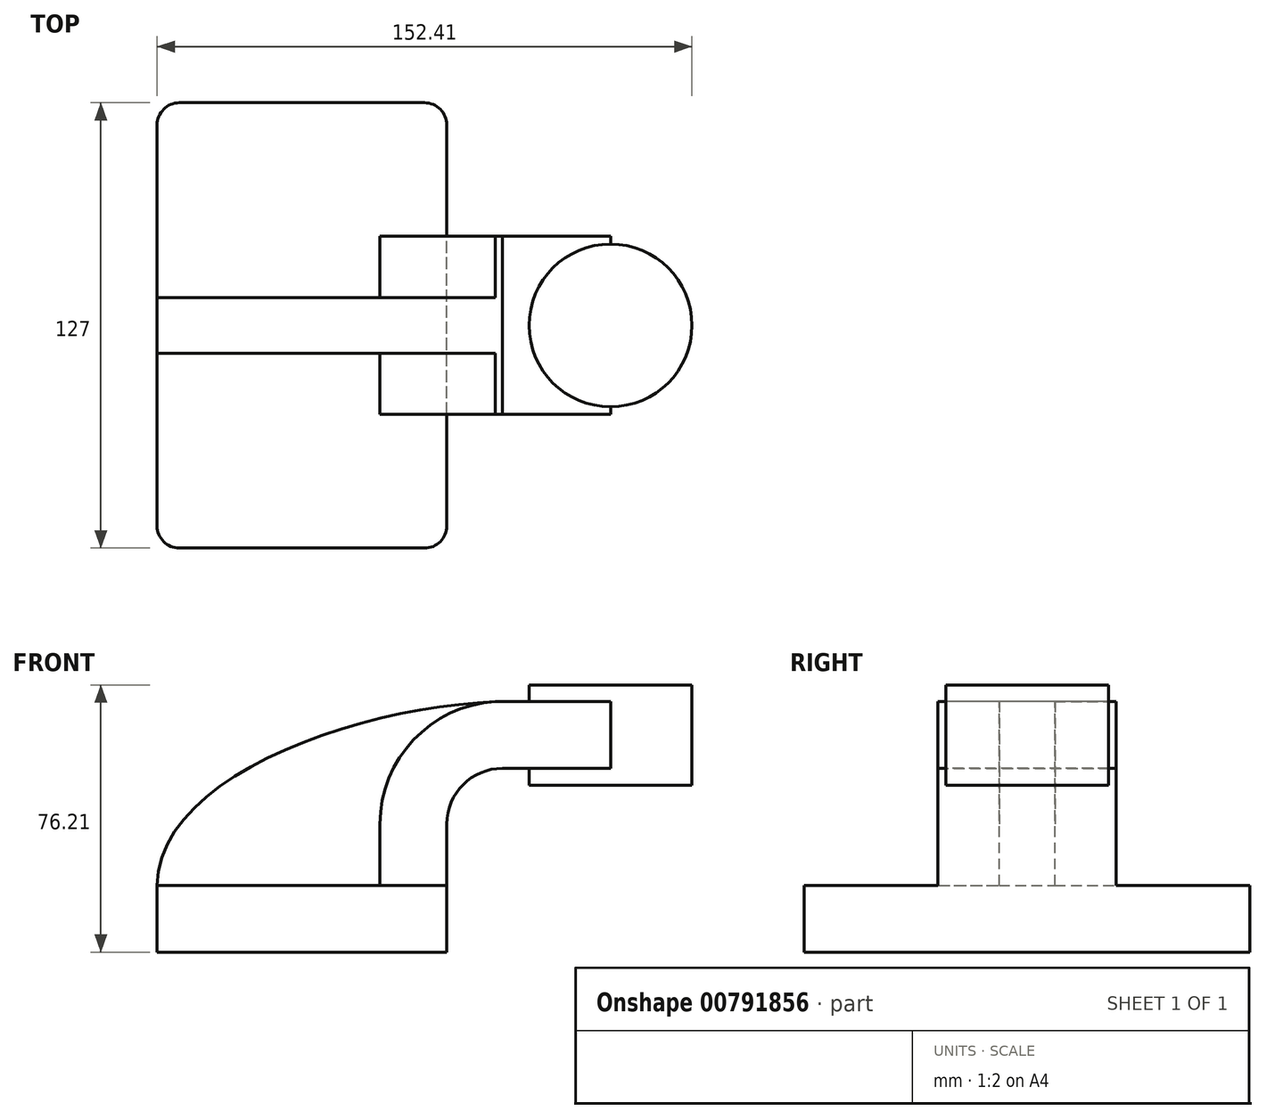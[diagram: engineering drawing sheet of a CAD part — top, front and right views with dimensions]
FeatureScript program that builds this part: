
annotation { "Feature Type Name" : "Feature", "Feature Type Description" : "" }
export const myFeature = defineFeature(function(context is Context, id is Id, definition is map)
    precondition{}
    {
        {
            var Q0;
            Q0=qCreatedBy(makeId("Front.planeOp"),FACE);
            var sketch = newSketch(context, id + "F0", { "sketchPlane" : qUnion([Q0])});
            skLineSegment(sketch, "E0.bottom", {"start": v(-41.28, 9.52) * mm, "end": v(41.27, 9.53) * mm});
            skLineSegment(sketch, "E0.top", {"start": v(-41.28, -9.53) * mm, "end": v(41.28, -9.53) * mm});
            skLineSegment(sketch, "E0.left", {"start": v(-41.28, 9.52) * mm, "end": v(-41.27, -9.53) * mm});
            skLineSegment(sketch, "E0.right", {"start": v(41.28, 9.53) * mm, "end": v(41.28, -9.52) * mm});
            skPoint(sketch, "E0.middle", {"position": v(0, 0) * mm});
            skLineSegment(sketch, "E1.bottom", {"start": v(60.33, 66.67) * mm, "end": v(111.12, 66.67) * mm});
            skLineSegment(sketch, "E1.top", {"start": v(60.33, 38.1) * mm, "end": v(111.12, 38.1) * mm});
            skLineSegment(sketch, "E1.left", {"start": v(60.33, 66.67) * mm, "end": v(60.33, 38.1) * mm});
            skLineSegment(sketch, "E1.right", {"start": v(111.12, 66.67) * mm, "end": v(111.12, 38.1) * mm});
            skLineSegment(sketch, "E2", {"start": v(41.27, 9.53) * mm, "end": v(41.27, 27) * mm});
            skArc(sketch, "E3", {"start": v(41.27, 27) * mm, "mid": v(45.92, 38.23) * mm, "end": v(57.15, 42.88) * mm});
            skLineSegment(sketch, "E4", {"start": v(57.15, 42.88) * mm, "end": v(87.93, 42.88) * mm});
            skLineSegment(sketch, "E5.0", {"start": v(57.15, 61.93) * mm, "end": v(87.93, 61.93) * mm});
            skArc(sketch, "E5.1", {"start": v(22.22, 27) * mm, "mid": v(32.45, 51.7) * mm, "end": v(57.15, 61.93) * mm});
            skLineSegment(sketch, "E5.2", {"start": v(22.22, 9.53) * mm, "end": v(22.22, 27) * mm});
            skLineSegment(sketch, "E6", {"start": v(87.93, 66.67) * mm, "end": v(87.93, 38.1) * mm});
            skPoint(sketch, "E6.endSnap0", {"position": v(85.72, 38.1) * mm});
            skFitSpline(sketch, "E7", {"points": [v(-41.28, 9.53) * mm, v(57.15, 61.93) * mm], "startDerivative": vector(1.06, 96.1) * mm, "endDerivative": vector(115.65, 2.42) * mm});
            skSolve(sketch);
        }
        {
            var Q0;
            Q0=makeQuery(id+"F0.imprint","IMPRINT",FACE,{"disambiguationData":[TD([[makeQuery(id+"F0.imprint","IMPRINT",EDGE,{"derivedFrom":sQuery(id+"F0.wireOp",EDGE,"E0.top")}),1.0]])]});
            extrude(context, id + "F1", {"entities" : qUnion([Q0]), "endBound" : BoundingType.SYMMETRIC, "depth" : 127 * mm, "offsetDistance" : 25.4 * mm});
        }
        {
            var Q0;
            {var subQ1=sQuery(id+"F0.wireOp",EDGE,"E2");Q0=makeQuery(id+"F0.imprint","IMPRINT",FACE,{"disambiguationData":[TD([[makeQuery(id+"F0.imprint","IMPRINT",EDGE,{"derivedFrom":subQ1}),1.0]])]});}
            var Q1;
            {var subQ0=sQuery(id+"F0.wireOp",EDGE,"E5.0");var subQ1=sQuery(id+"F0.wireOp",EDGE,"E1.left");var subQ2=makeQuery(id+"F0.imprint","INTERSECT",VERTEX,{"derivedFrom":[subQ1,subQ0]});Q1=makeQuery(id+"F0.imprint","IMPRINT",FACE,{"disambiguationData":[TD([[makeQuery(id+"F0.imprint","IMPRINT",EDGE,{"disambiguationData":[TD([[subQ2,-1.0]])],"derivedFrom":subQ1}),1.0]])]});}
            extrude(context, id + "F2", {"entities" : qUnion([Q0, Q1]), "operationType" : NewBodyOperationType.ADD, "endBound" : BoundingType.SYMMETRIC, "depth" : 50.8 * mm, "offsetDistance" : 25.4 * mm});
        }
        {
            var Q0;
            {var subQ3=sQuery(id+"F0.wireOp",EDGE,"E5.2");Q0=makeQuery(id+"F0.imprint","IMPRINT",FACE,{"disambiguationData":[TD([[makeQuery(id+"F0.imprint","IMPRINT",EDGE,{"derivedFrom":subQ3}),1.0]])]});}
            extrude(context, id + "F3", {"entities" : qUnion([Q0]), "operationType" : NewBodyOperationType.ADD, "endBound" : BoundingType.SYMMETRIC, "depth" : 15.88 * mm, "offsetDistance" : 25.4 * mm});
        }
        {
            var Q0;
            {var subQ4=sQuery(id+"F0.wireOp",EDGE,"E1.right");Q0=makeQuery(id+"F0.imprint","IMPRINT",FACE,{"disambiguationData":[TD([[makeQuery(id+"F0.imprint","IMPRINT",EDGE,{"derivedFrom":subQ4}),-1.0]])]});}
            var Q1;
            Q1=sQuery(id+"F0.wireOp",EDGE,"E6");
            revolve(context, id + "F4", {"operationType" : NewBodyOperationType.ADD, "surfaceOperationType" : NewSurfaceOperationType.NEW, "entities" : qUnion([Q0]), "axis" : qUnion([Q1]), "revolveType" : RevolveType.FULL});
        }
        {
            var Q0;
            Q0=makeQuery(id+"F1.opExtrude","CAP_EDGE",EDGE,{"disambiguationData":[OSD([sQuery(id+"F0.wireOp",EDGE,"E0.left")])],"isStart":false});
            var Q1;
            Q1=makeQuery(id+"F1.opExtrude","CAP_EDGE",EDGE,{"disambiguationData":[OSD([sQuery(id+"F0.wireOp",EDGE,"E0.right")])],"isStart":false});
            var Q2;
            Q2=makeQuery(id+"F1.opExtrude","CAP_EDGE",EDGE,{"disambiguationData":[OSD([sQuery(id+"F0.wireOp",EDGE,"E0.right")])],"isStart":true});
            var Q3;
            Q3=makeQuery(id+"F1.opExtrude","CAP_EDGE",EDGE,{"disambiguationData":[OSD([sQuery(id+"F0.wireOp",EDGE,"E0.left")])],"isStart":true});
            fillet(context, id + "F5", {"entities" : qUnion([Q0, Q1, Q2, Q3]), "radius" : 6.35 * mm, "tangentPropagation" : true, "allowEdgeOverflow" : false});
        }
    });
